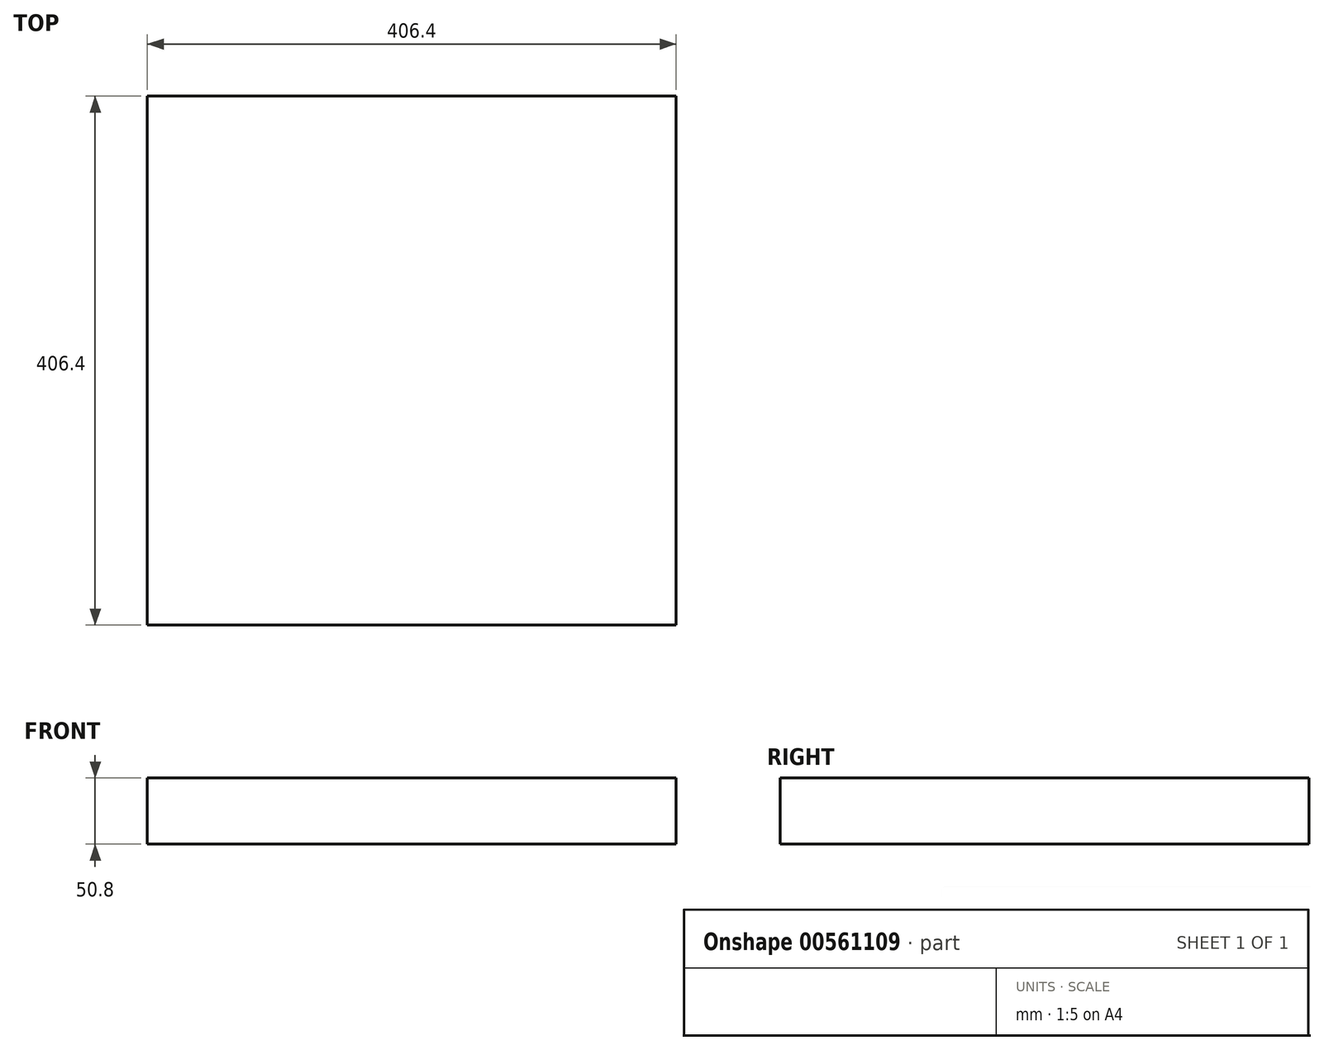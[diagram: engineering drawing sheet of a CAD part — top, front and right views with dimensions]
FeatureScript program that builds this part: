
annotation { "Feature Type Name" : "Feature", "Feature Type Description" : "" }
export const myFeature = defineFeature(function(context is Context, id is Id, definition is map)
    precondition{}
    {
        {
            var Q0;
            Q0=qCreatedBy(makeId("Top.planeOp"),FACE);
            var sketch = newSketch(context, id + "F0", { "sketchPlane" : qUnion([Q0])});
            skLineSegment(sketch, "E0.bottom", {"start": v(0, 0) * mm, "end": v(406.4, 0) * mm});
            skLineSegment(sketch, "E0.top", {"start": v(0, 406.4) * mm, "end": v(406.4, 406.4) * mm});
            skLineSegment(sketch, "E0.left", {"start": v(0, 0) * mm, "end": v(0, 406.4) * mm});
            skLineSegment(sketch, "E0.right", {"start": v(406.4, 0) * mm, "end": v(406.4, 406.4) * mm});
            skSolve(sketch);
        }
        {
            var Q0;
            Q0=makeQuery(id+"F0.imprint","IMPRINT",FACE,{"disambiguationData":[TD([[makeQuery(id+"F0.imprint","IMPRINT",EDGE,{"derivedFrom":sQuery(id+"F0.wireOp",EDGE,"E0.bottom")}),1.0]])]});
            extrude(context, id + "F1", {"entities" : qUnion([Q0]), "depth" : 50.8 * mm, "offsetDistance" : 25.4 * mm});
        }
    });
